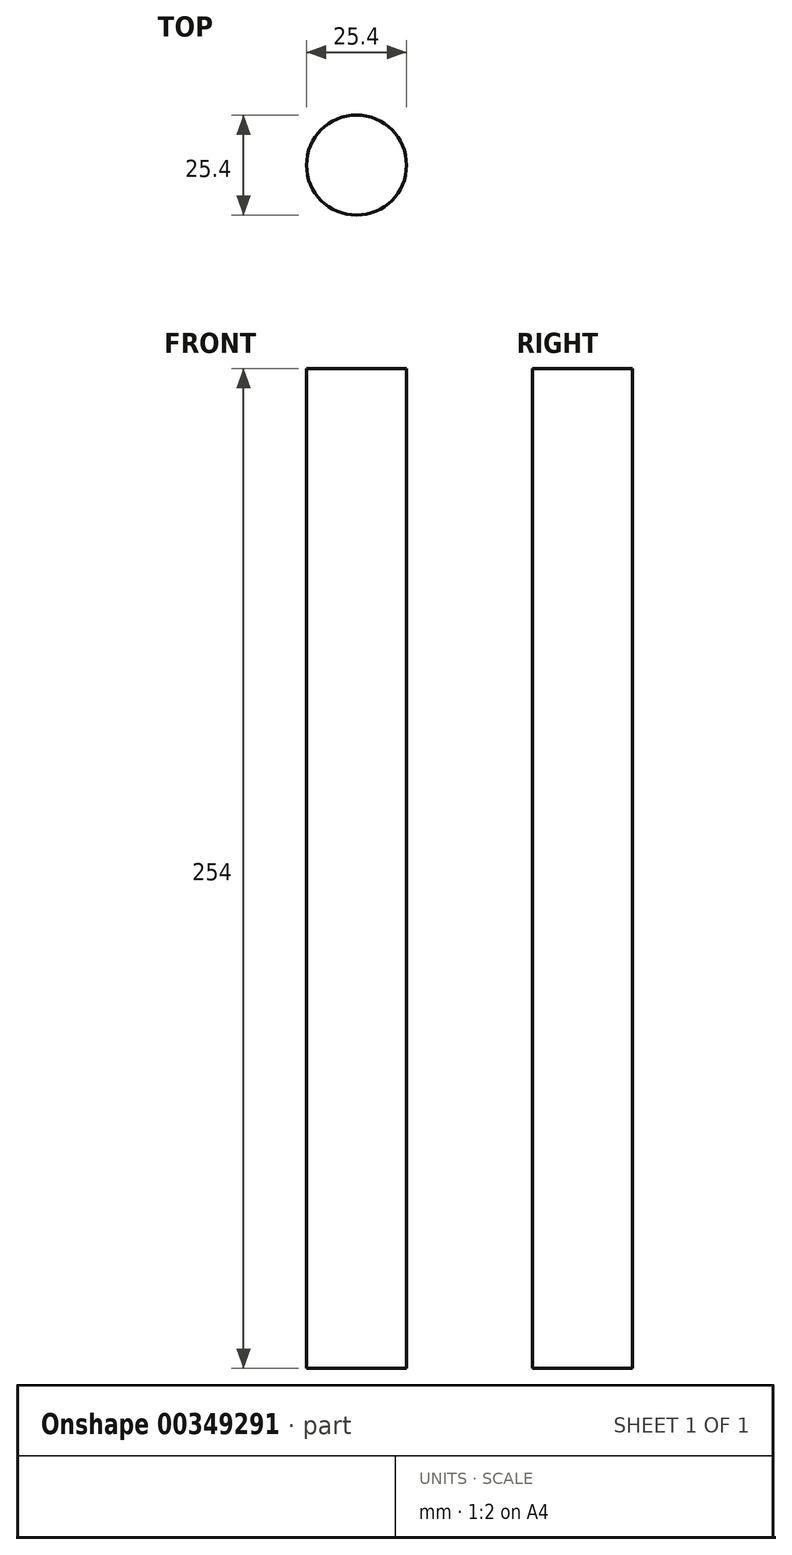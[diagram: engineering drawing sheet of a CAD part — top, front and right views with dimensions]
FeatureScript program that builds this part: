
annotation { "Feature Type Name" : "Feature", "Feature Type Description" : "" }
export const myFeature = defineFeature(function(context is Context, id is Id, definition is map)
    precondition{}
    {
        {
            var Q0;
            Q0=qCreatedBy(makeId("Top.planeOp"),FACE);
            cPlane(context, id + "F0", {"entities" : qUnion([Q0]), "cplaneType" : CPlaneType.OFFSET, "offset" : 254 * mm, "width" : 152.4 * mm, "height" : 152.4 * mm});
        }
        {
            var Q0;
            Q0=qCreatedBy(makeId("Top.planeOp"),FACE);
            var sketch = newSketch(context, id + "F1", { "sketchPlane" : qUnion([Q0])});
            skCircle(sketch, "E0", {"center": v(0, 0) * mm, "radius": 12.7 * mm});
            skSolve(sketch);
        }
        {
            var Q0;
            Q0=qCreatedBy(id+"F0.planeOp",FACE);
            var sketch = newSketch(context, id + "F2", { "sketchPlane" : qUnion([Q0])});
            skCircle(sketch, "E1", {"center": v(0, 0) * mm, "radius": 12.7 * mm});
            skSolve(sketch);
        }
        {
            var Q0;
            Q0=makeQuery(id+"F2.imprint","IMPRINT",FACE,{"disambiguationData":[TD([[makeQuery(id+"F2.imprint","IMPRINT",EDGE,{"derivedFrom":sQuery(id+"F2.wireOp",EDGE,"E1")}),1.0]])]});
            var Q1;
            Q1=makeQuery(id+"F1.imprint","IMPRINT",FACE,{"disambiguationData":[TD([[makeQuery(id+"F1.imprint","IMPRINT",EDGE,{"derivedFrom":sQuery(id+"F1.wireOp",EDGE,"E0")}),1.0]])]});
            loft(context, id + "F3", {"sheetProfilesArray" : [{ "sheetProfileEntities" : qUnion([Q0]) }, { "sheetProfileEntities" : qUnion([Q1]) }]});
        }
    });
